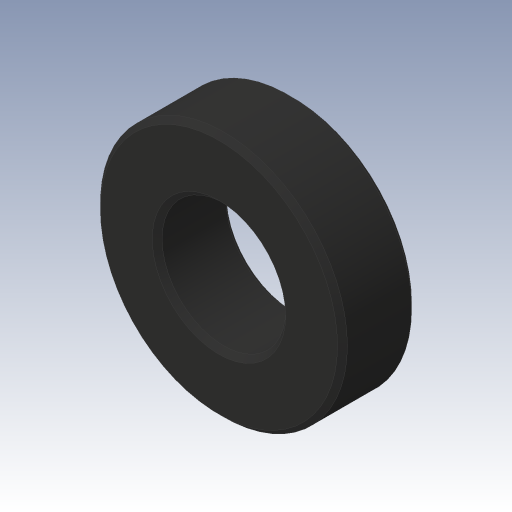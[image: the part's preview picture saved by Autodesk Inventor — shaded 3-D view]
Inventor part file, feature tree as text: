
AUTODESK INVENTOR PART (.ipt)
format: ipt  version: 2023.3 (Build 273359000, 359)  size: 144,384 bytes
history: native  units: in
note: dims shown in document units (in); Inventor stores cm internally (conversion verified against a paired STEP export)
features: extrude x1, chamfer x1, sketch x1
ambient origin geometry x8: Origin, YZ Plane, XZ Plane, XY Plane, X Axis, Y Axis, Z Axis, Center Point
bodies: Body1 (feature_tree)
feature tree (3):
  extrude  "Extrusion3"  Depth=0.3937in
  chamfer  "Fase1"  Distance=0.1181in
  sketch  "Skizze3"  dims[d4=0.1969in d5=0.3937in d6=0.1181in d7=0.0in d8=0.0079in d9=0.0787in d10=45.0deg]
